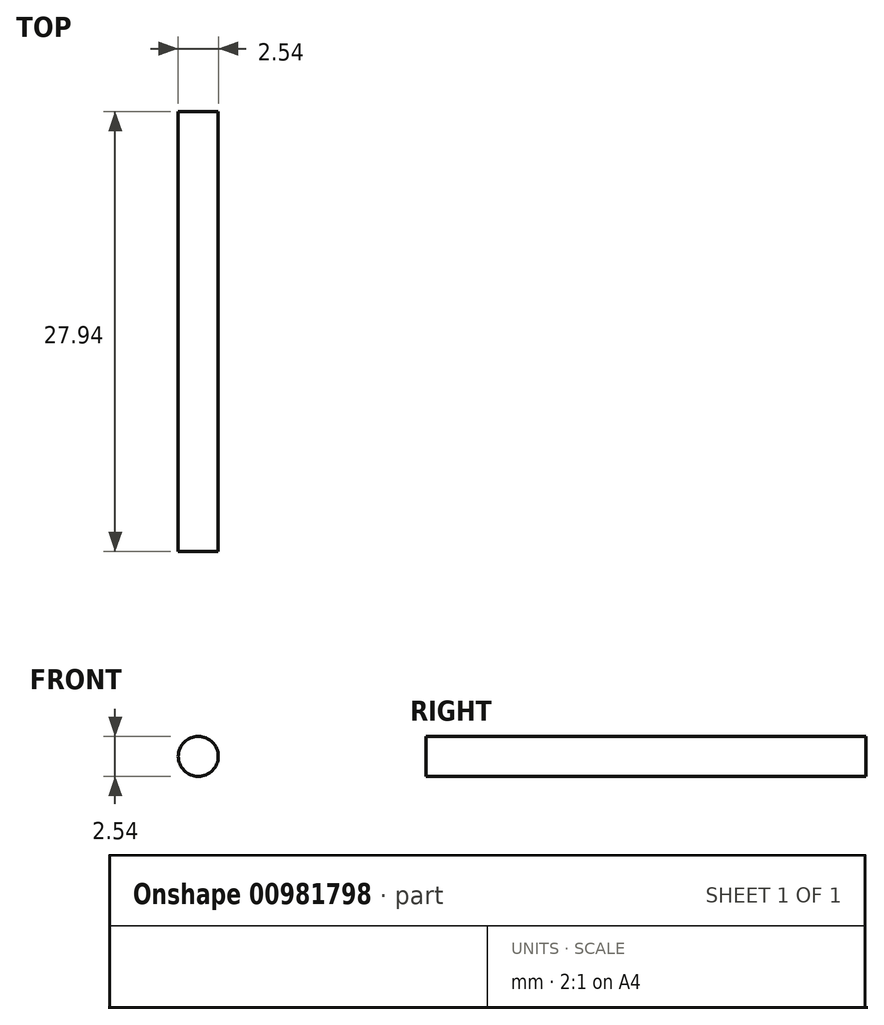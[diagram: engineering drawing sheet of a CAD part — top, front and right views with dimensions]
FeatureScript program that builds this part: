
annotation { "Feature Type Name" : "Feature", "Feature Type Description" : "" }
export const myFeature = defineFeature(function(context is Context, id is Id, definition is map)
    precondition{}
    {
        {
            var Q0;
            Q0=qCreatedBy(makeId("Front.planeOp"),FACE);
            var sketch = newSketch(context, id + "F0", { "sketchPlane" : qUnion([Q0])});
            skCircle(sketch, "E0", {"center": v(-36.75, 7.27) * mm, "radius": 1.27 * mm});
            skSolve(sketch);
        }
        {
            var Q0;
            Q0=makeQuery(id+"F0.imprint","IMPRINT",FACE,{"disambiguationData":[TD([[makeQuery(id+"F0.imprint","IMPRINT",EDGE,{"derivedFrom":sQuery(id+"F0.wireOp",EDGE,"E0")}),1.0]])]});
            extrude(context, id + "F1", {"entities" : qUnion([Q0]), "depth" : 27.94 * mm, "offsetDistance" : 25.4 * mm});
        }
    });
